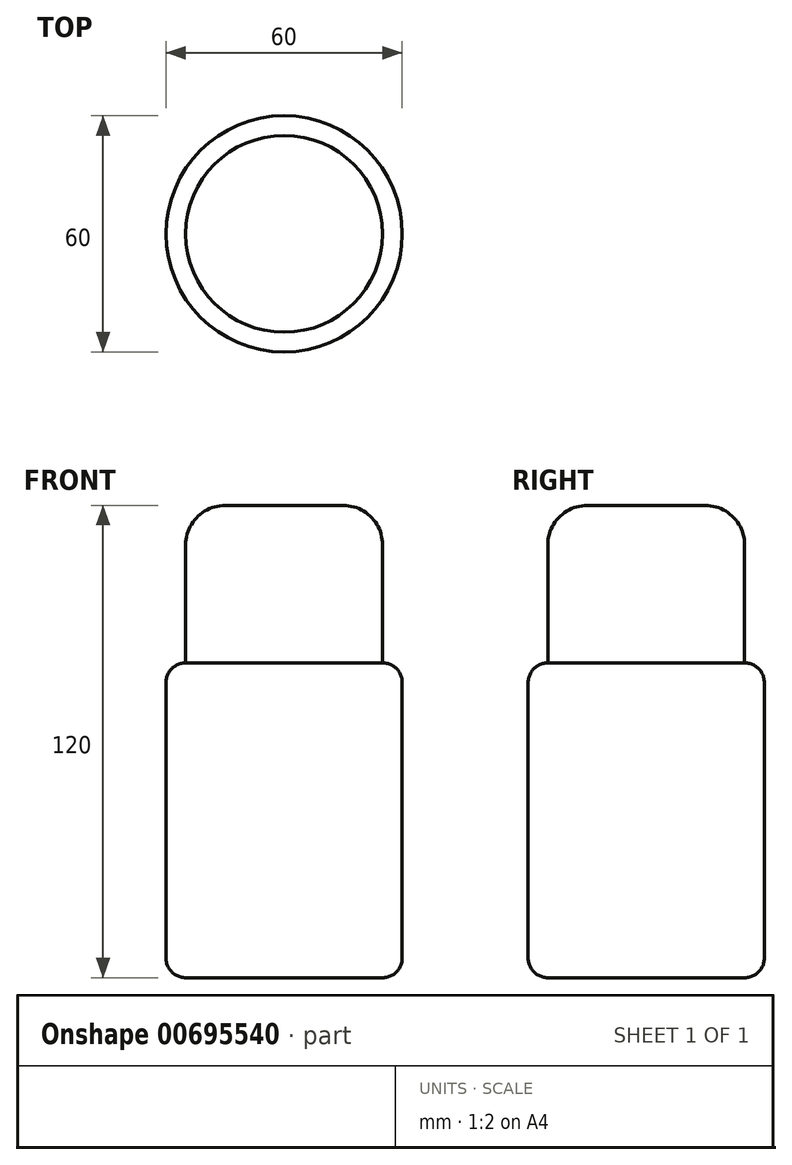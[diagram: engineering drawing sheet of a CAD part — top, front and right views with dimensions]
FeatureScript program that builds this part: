
annotation { "Feature Type Name" : "Feature", "Feature Type Description" : "" }
export const myFeature = defineFeature(function(context is Context, id is Id, definition is map)
    precondition{}
    {
        {
            var Q0;
            Q0=qCreatedBy(makeId("Top.planeOp"),FACE);
            var sketch = newSketch(context, id + "F0", { "sketchPlane" : qUnion([Q0])});
            skCircle(sketch, "E0", {"center": v(0, 0) * mm, "radius": 30 * mm});
            skSolve(sketch);
        }
        {
            var Q0;
            Q0 = qSketchRegion(id + "F0", true);
            extrude(context, id + "F1", {"entities" : qUnion([Q0]), "depth" : 80 * mm, "offsetDistance" : 25 * mm});
        }
        {
            var Q0;
            Q0=makeQuery(id+"F1.opExtrude","CAP_FACE",FACE,{"disambiguationData":[OSD([sQuery(id+"F0.wireOp",EDGE,"E0")])],"isStart":false});
            var sketch = newSketch(context, id + "F2", { "sketchPlane" : qUnion([Q0])});
            skCircle(sketch, "E1", {"center": v(0, 0) * mm, "radius": 25 * mm});
            skSolve(sketch);
        }
        {
            var Q0;
            Q0=makeQuery(id+"F2.imprint","IMPRINT",FACE,{"disambiguationData":[TD([[makeQuery(id+"F2.imprint","IMPRINT",EDGE,{"derivedFrom":sQuery(id+"F2.wireOp",EDGE,"E1")}),1.0]])]});
            extrude(context, id + "F3", {"entities" : qUnion([Q0]), "operationType" : NewBodyOperationType.ADD, "depth" : 40 * mm, "offsetDistance" : 25 * mm});
        }
        {
            var Q0;
            Q0=makeQuery(id+"F1.opExtrude","CAP_EDGE",EDGE,{"disambiguationData":[OSD([sQuery(id+"F0.wireOp",EDGE,"E0")])],"isStart":false});
            fillet(context, id + "F4", {"entities" : qUnion([Q0]), "radius" : 5 * mm, "tangentPropagation" : true, "allowEdgeOverflow" : false});
        }
        {
            var Q0;
            Q0=makeQuery(id+"F1.opExtrude","CAP_EDGE",EDGE,{"disambiguationData":[OSD([sQuery(id+"F0.wireOp",EDGE,"E0")])],"isStart":true});
            fillet(context, id + "F5", {"entities" : qUnion([Q0]), "radius" : 5 * mm, "tangentPropagation" : true, "allowEdgeOverflow" : false});
        }
        {
            var Q0;
            Q0=makeQuery(id+"F3.opExtrude","CAP_EDGE",EDGE,{"disambiguationData":[OSD([sQuery(id+"F2.wireOp",EDGE,"E1")])],"isStart":false});
            fillet(context, id + "F6", {"entities" : qUnion([Q0]), "radius" : 10 * mm, "tangentPropagation" : true, "allowEdgeOverflow" : false});
        }
    });
